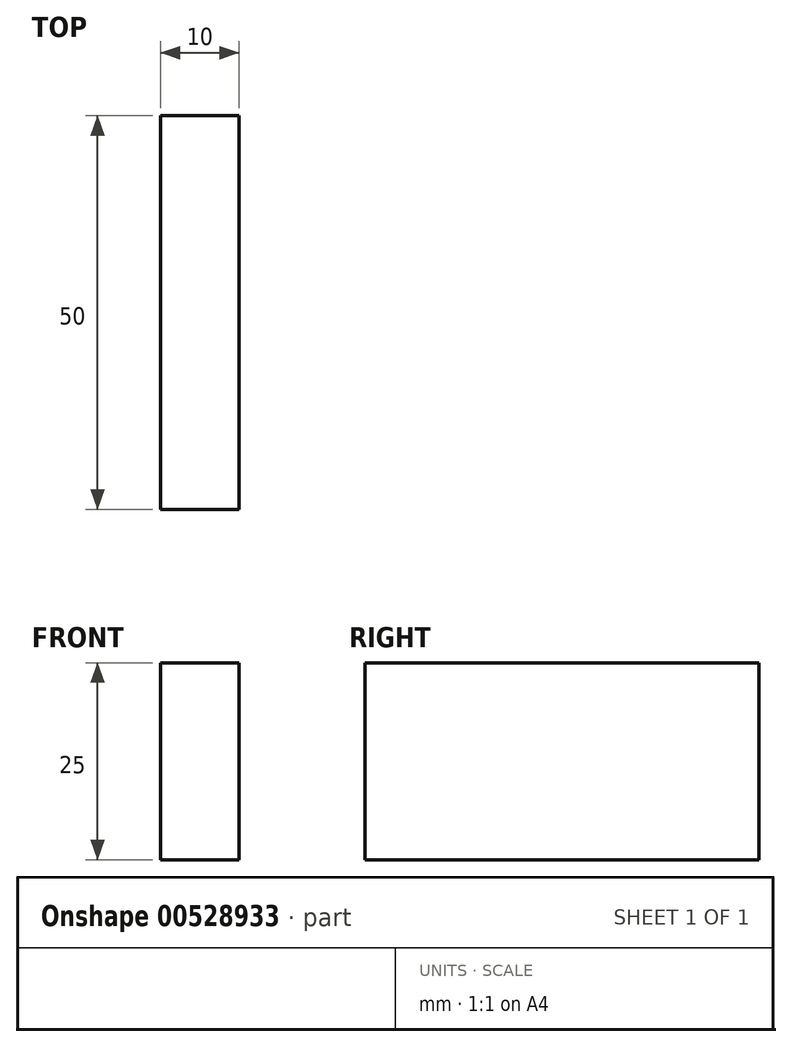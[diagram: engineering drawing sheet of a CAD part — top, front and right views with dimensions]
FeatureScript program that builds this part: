
annotation { "Feature Type Name" : "Feature", "Feature Type Description" : "" }
export const myFeature = defineFeature(function(context is Context, id is Id, definition is map)
    precondition{}
    {
        {
            var Q0;
            Q0=qCreatedBy(makeId("Top.planeOp"),FACE);
            var sketch = newSketch(context, id + "F0", { "sketchPlane" : qUnion([Q0])});
            skLineSegment(sketch, "E0.bottom", {"start": v(-57.89, 39.45) * mm, "end": v(-67.89, 39.45) * mm});
            skLineSegment(sketch, "E0.top", {"start": v(-57.89, 89.45) * mm, "end": v(-67.89, 89.45) * mm});
            skLineSegment(sketch, "E0.left", {"start": v(-57.89, 39.45) * mm, "end": v(-57.89, 89.45) * mm});
            skLineSegment(sketch, "E0.right", {"start": v(-67.89, 39.45) * mm, "end": v(-67.89, 89.45) * mm});
            skPoint(sketch, "E0.middle", {"position": v(-62.89, 64.45) * mm});
            skSolve(sketch);
        }
        {
            var Q0;
            Q0 = qSketchRegion(id + "F0", true);
            extrude(context, id + "F1", {"entities" : qUnion([Q0]), "depth" : 25 * mm, "offsetDistance" : 25 * mm});
        }
    });
